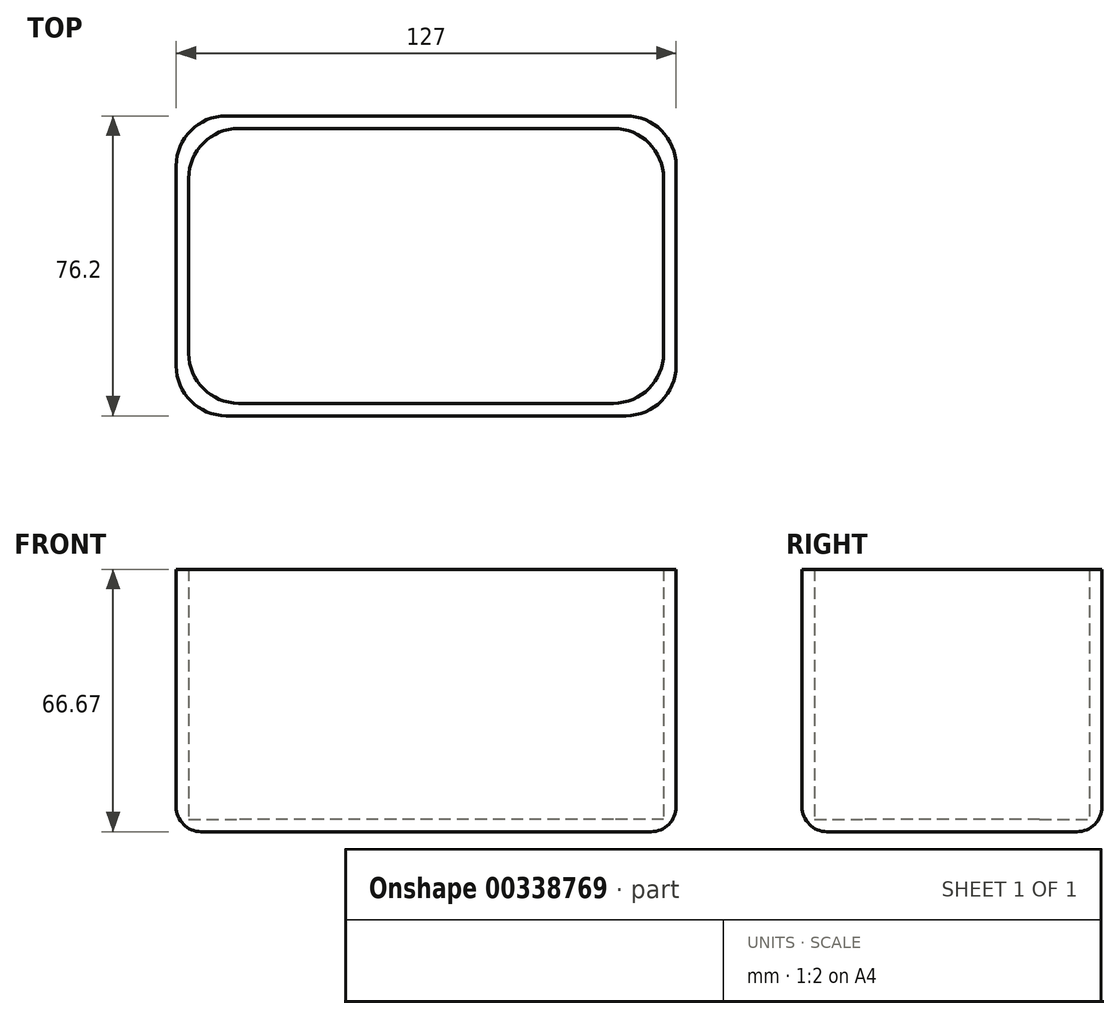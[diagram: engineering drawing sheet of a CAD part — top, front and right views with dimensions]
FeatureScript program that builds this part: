
annotation { "Feature Type Name" : "Feature", "Feature Type Description" : "" }
export const myFeature = defineFeature(function(context is Context, id is Id, definition is map)
    precondition{}
    {
        {
            var Q0;
            Q0=qCreatedBy(makeId("Top.planeOp"),FACE);
            var sketch = newSketch(context, id + "F0", { "sketchPlane" : qUnion([Q0])});
            skLineSegment(sketch, "E0.bottom", {"start": v(50.8, 38.1) * mm, "end": v(-50.8, 38.1) * mm});
            skLineSegment(sketch, "E0.top", {"start": v(50.8, -38.1) * mm, "end": v(-50.8, -38.1) * mm});
            skLineSegment(sketch, "E0.left", {"start": v(63.5, 25.4) * mm, "end": v(63.5, -25.4) * mm});
            skLineSegment(sketch, "E0.right", {"start": v(-63.5, 25.4) * mm, "end": v(-63.5, -25.4) * mm});
            skPoint(sketch, "E0.middle", {"position": v(0, 0) * mm});
            skLineSegment(sketch, "E1.0", {"start": v(47.62, 34.93) * mm, "end": v(-47.62, 34.93) * mm});
            skLineSegment(sketch, "E1.1", {"start": v(60.33, 22.23) * mm, "end": v(60.33, -22.23) * mm});
            skLineSegment(sketch, "E1.2", {"start": v(47.62, -34.93) * mm, "end": v(-47.62, -34.93) * mm});
            skLineSegment(sketch, "E1.3", {"start": v(-60.33, 22.23) * mm, "end": v(-60.33, -22.23) * mm});
            skPoint(sketch, "E2.visualSharp", {"position": v(-60.33, 34.93) * mm});
            skArc(sketch, "E2.filletArc", {"start": v(-47.62, 34.93) * mm, "mid": v(-56.6, 31.2) * mm, "end": v(-60.33, 22.23) * mm});
            skPoint(sketch, "E3.visualSharp", {"position": v(-63.5, 38.1) * mm});
            skArc(sketch, "E3.filletArc", {"start": v(-50.8, 38.1) * mm, "mid": v(-59.78, 34.38) * mm, "end": v(-63.5, 25.4) * mm});
            skPoint(sketch, "E4.visualSharp", {"position": v(60.33, 34.93) * mm});
            skArc(sketch, "E4.filletArc", {"start": v(60.33, 22.23) * mm, "mid": v(56.6, 31.2) * mm, "end": v(47.62, 34.93) * mm});
            skPoint(sketch, "E5.visualSharp", {"position": v(63.5, 38.1) * mm});
            skArc(sketch, "E5.filletArc", {"start": v(63.5, 25.4) * mm, "mid": v(59.78, 34.38) * mm, "end": v(50.8, 38.1) * mm});
            skPoint(sketch, "E6.visualSharp", {"position": v(60.33, -34.93) * mm});
            skArc(sketch, "E6.filletArc", {"start": v(47.62, -34.93) * mm, "mid": v(56.6, -31.2) * mm, "end": v(60.33, -22.23) * mm});
            skPoint(sketch, "E7.visualSharp", {"position": v(63.5, -38.1) * mm});
            skArc(sketch, "E7.filletArc", {"start": v(50.8, -38.1) * mm, "mid": v(59.78, -34.38) * mm, "end": v(63.5, -25.4) * mm});
            skPoint(sketch, "E8.visualSharp", {"position": v(-60.33, -34.93) * mm});
            skArc(sketch, "E8.filletArc", {"start": v(-60.33, -22.23) * mm, "mid": v(-56.6, -31.2) * mm, "end": v(-47.62, -34.93) * mm});
            skPoint(sketch, "E9.visualSharp", {"position": v(-63.5, -38.1) * mm});
            skArc(sketch, "E9.filletArc", {"start": v(-63.5, -25.4) * mm, "mid": v(-59.78, -34.38) * mm, "end": v(-50.8, -38.1) * mm});
            skSolve(sketch);
        }
        {
            var Q0;
            Q0=makeQuery(id+"F0.imprint","IMPRINT",FACE,{"disambiguationData":[TD([[makeQuery(id+"F0.imprint","IMPRINT",EDGE,{"derivedFrom":sQuery(id+"F0.wireOp",EDGE,"E1.0")}),1.0]])]});
            var Q1;
            Q1=makeQuery(id+"F0.imprint","IMPRINT",FACE,{"disambiguationData":[TD([[makeQuery(id+"F0.imprint","IMPRINT",EDGE,{"derivedFrom":sQuery(id+"F0.wireOp",EDGE,"E0.bottom")}),1.0]])]});
            extrude(context, id + "F1", {"entities" : qUnion([Q0, Q1]), "depth" : -3.17 * mm});
        }
        {
            var Q0;
            Q0 = qSketchRegion(id + "F0", true);
            extrude(context, id + "F2", {"entities" : qUnion([Q0]), "operationType" : NewBodyOperationType.ADD, "depth" : 63.5 * mm});
        }
        {
            var Q0;
            Q0=makeQuery(id+"F2.opExtrude","CAP_EDGE",EDGE,{"disambiguationData":[OSD([sQuery(id+"F0.wireOp",EDGE,"E1.0")])],"isStart":true});
            var Q1;
            Q1=makeQuery(id+"F1.opExtrude","CAP_EDGE",EDGE,{"disambiguationData":[OSD([sQuery(id+"F0.wireOp",EDGE,"E0.top")])],"isStart":false});
            fillet(context, id + "F3", {"entities" : qUnion([Q0, Q1]), "radius" : 6.35 * mm, "tangentPropagation" : true, "allowEdgeOverflow" : false});
        }
    });
